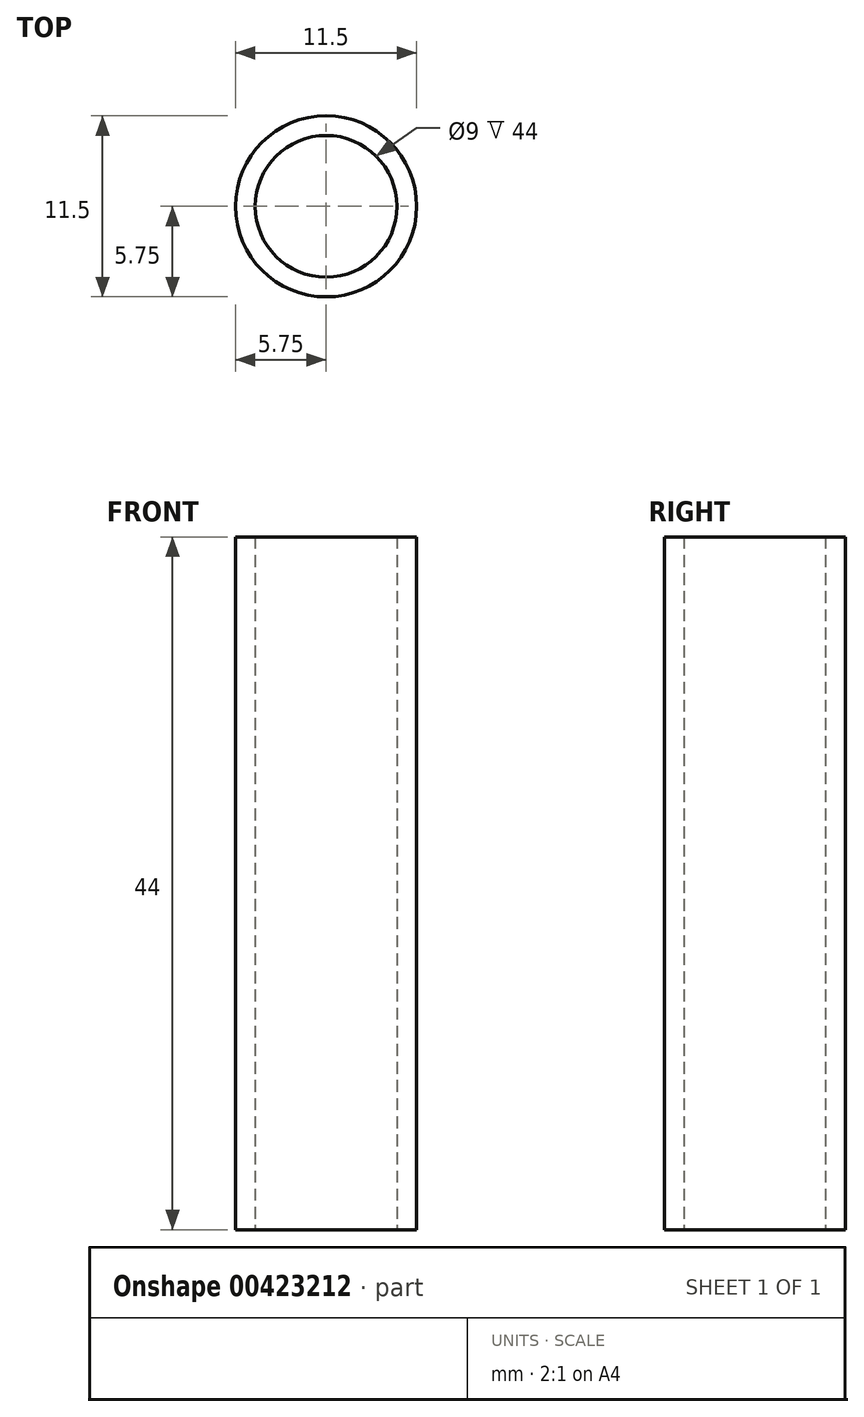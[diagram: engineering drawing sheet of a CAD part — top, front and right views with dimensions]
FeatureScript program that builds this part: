
annotation { "Feature Type Name" : "Feature", "Feature Type Description" : "" }
export const myFeature = defineFeature(function(context is Context, id is Id, definition is map)
    precondition{}
    {
        {
            var Q0;
            Q0=qCreatedBy(makeId("Top.planeOp"),FACE);
            var sketch = newSketch(context, id + "F0", { "sketchPlane" : qUnion([Q0])});
            skCircle(sketch, "E0", {"center": v(0, 0) * mm, "radius": 5.75 * mm});
            skCircle(sketch, "E1", {"center": v(0, 0) * mm, "radius": 4.5 * mm});
            skSolve(sketch);
        }
        {
            var Q0;
            Q0=makeQuery(id+"F0.imprint","IMPRINT",FACE,{"disambiguationData":[TD([[makeQuery(id+"F0.imprint","IMPRINT",EDGE,{"derivedFrom":sQuery(id+"F0.wireOp",EDGE,"E0")}),1.0]])]});
            extrude(context, id + "F1", {"entities" : qUnion([Q0]), "depth" : 44 * mm, "offsetDistance" : 25 * mm});
        }
    });
